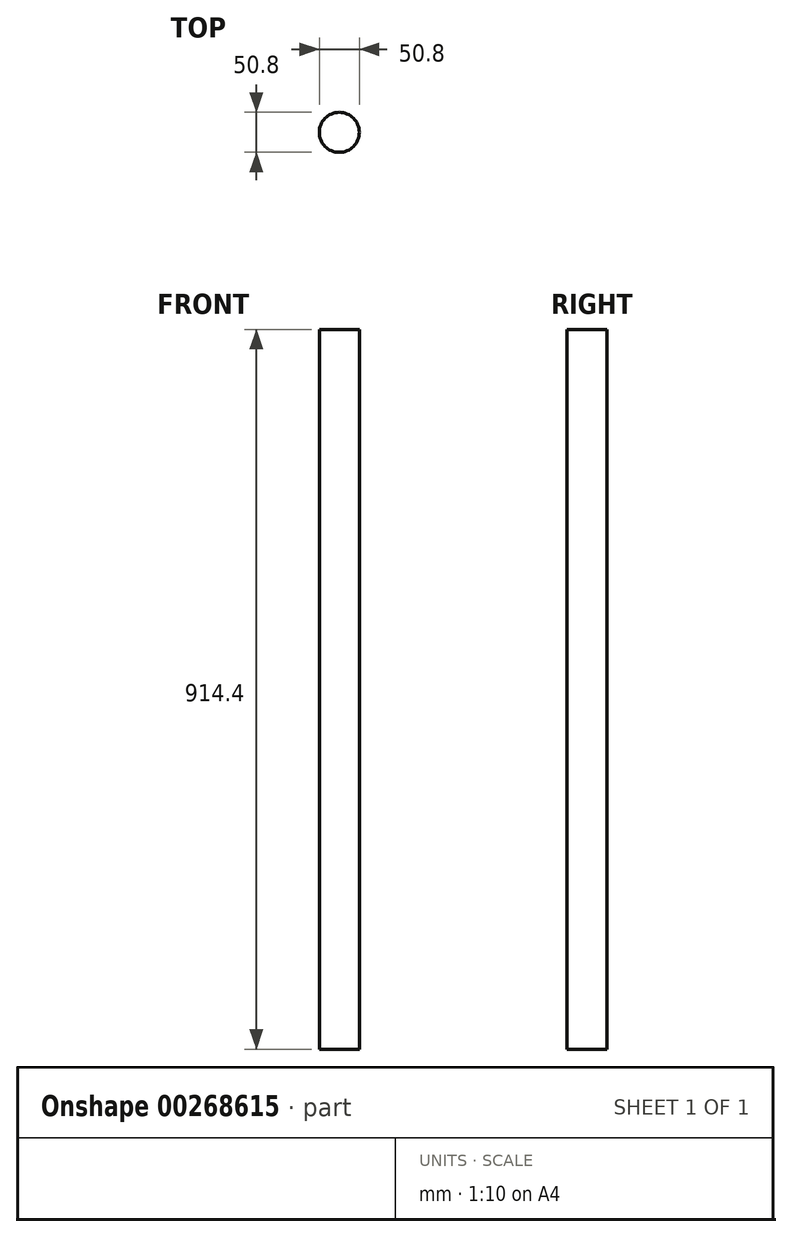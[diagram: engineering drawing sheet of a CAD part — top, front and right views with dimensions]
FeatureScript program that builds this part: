
annotation { "Feature Type Name" : "Feature", "Feature Type Description" : "" }
export const myFeature = defineFeature(function(context is Context, id is Id, definition is map)
    precondition{}
    {
        {
            var Q0;
            Q0=qCreatedBy(makeId("Top.planeOp"),FACE);
            var sketch = newSketch(context, id + "F0", { "sketchPlane" : qUnion([Q0])});
            skCircle(sketch, "E0", {"center": v(0, 0) * mm, "radius": 25.4 * mm});
            skSolve(sketch);
        }
        {
            var Q0;
            Q0=sQuery(id+"F0.wireOp",EDGE,"E0");
            extrude(context, id + "F1", {"bodyType" : ToolBodyType.SURFACE, "surfaceEntities" : qUnion([Q0]), "offsetDistance" : 25.4 * mm, "depth" : 914.4 * mm});
        }
    });
